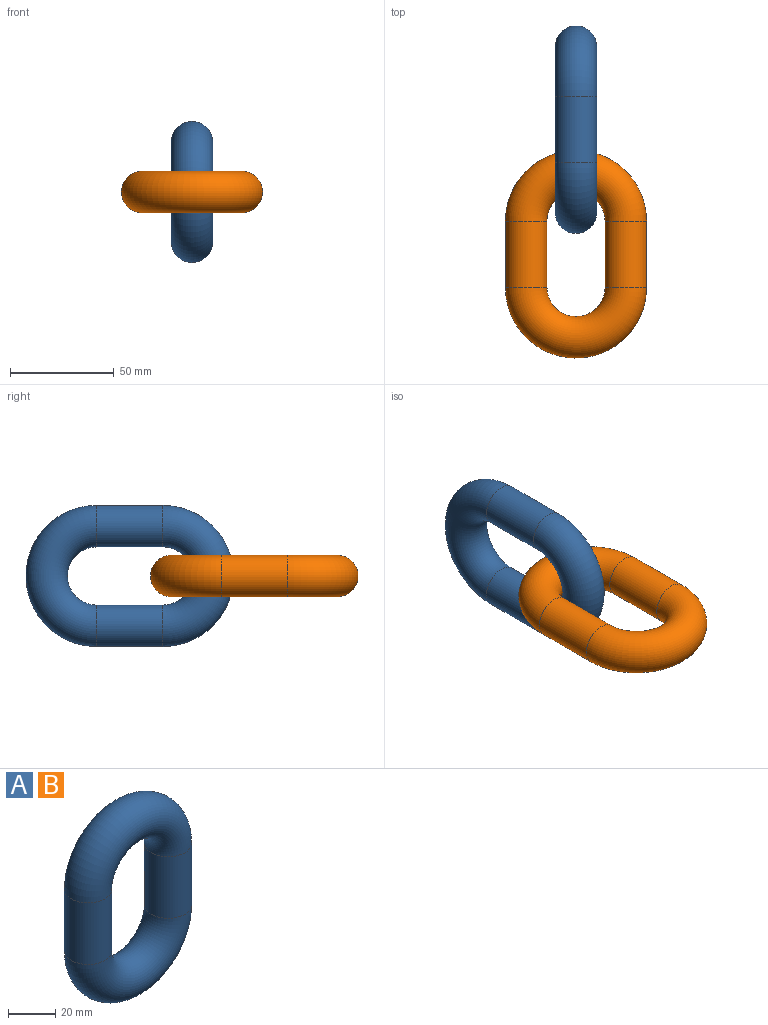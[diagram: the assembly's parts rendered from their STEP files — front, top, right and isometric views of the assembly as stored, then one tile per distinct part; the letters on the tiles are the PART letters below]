
ASSEMBLY  parts=2 mates=1
PART A: 4 faces, bbox 73.6x20x105.6 mm
  f0: torus R=24mm, axis (0,1,0), area 4737.4mm2, adj f1,f3
  f1: cylinder r=10mm len=32mm, axis (0,0,-1), area 2010.6mm2, adj f0,f2
  f2: torus R=24mm, axis (0,1,0), area 4737.4mm2, adj f1,f3
  f3: cylinder r=10mm len=32mm, axis (0,0,1), area 2010.6mm2, adj f0,f2
PART B: same geometry as A
PLACE A rot(axis=(0.58,-0.58,0.58),120deg) t=(0,30,0)mm
PLACE B rot(axis=(1,0,0),90deg) t=(0,-30,0)mm
MATE parallel A.f1 <-> B.f3  axis (0,1,0) through (0,30,24)mm
